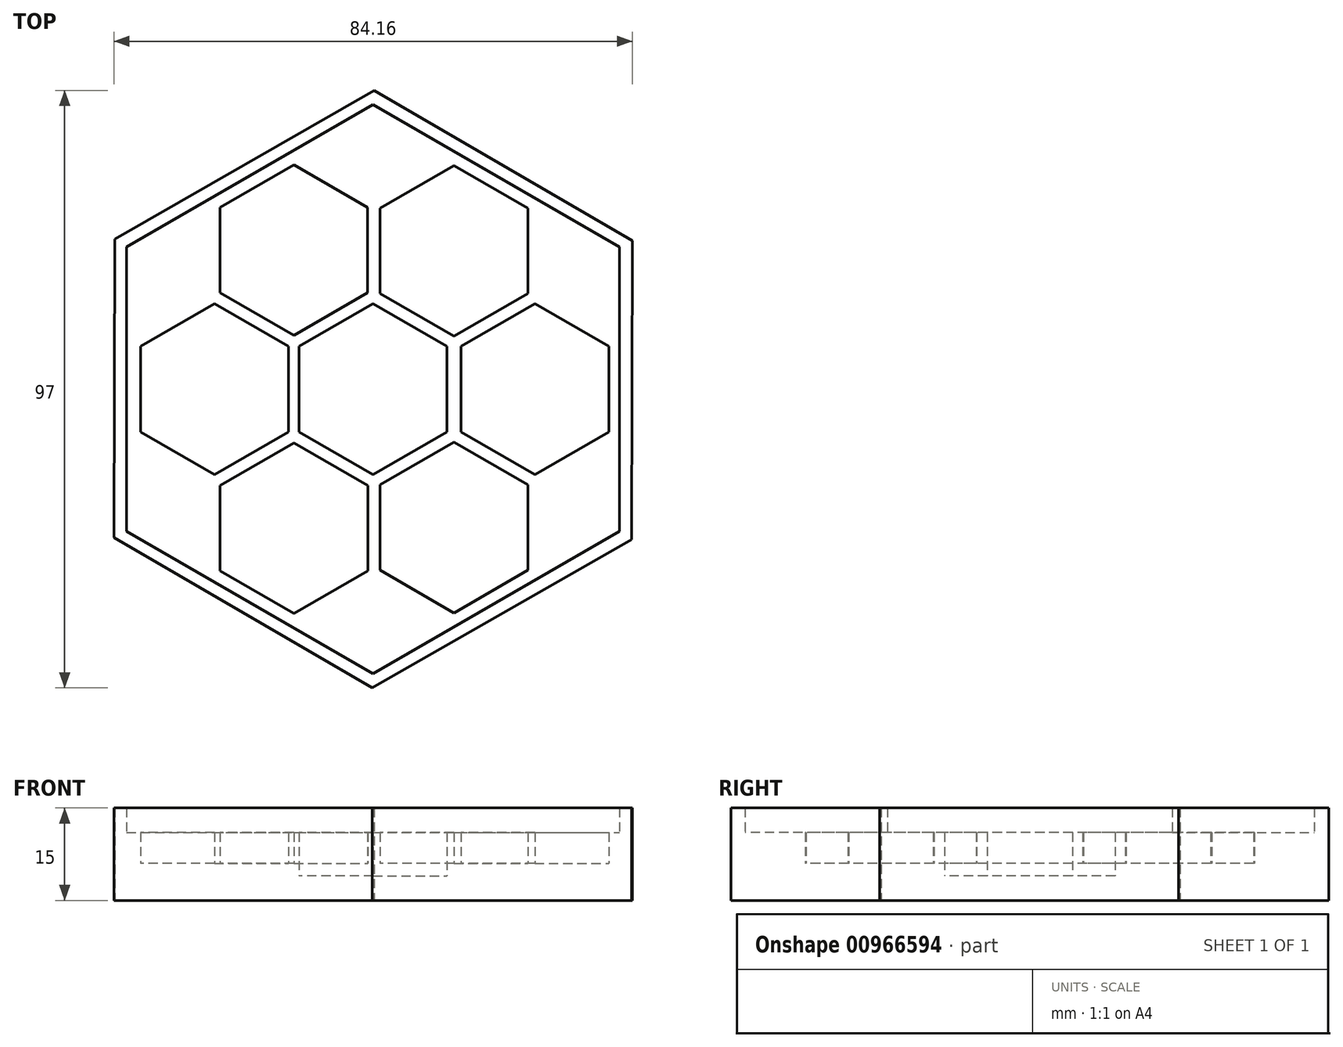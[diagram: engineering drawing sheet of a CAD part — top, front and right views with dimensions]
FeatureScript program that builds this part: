
annotation { "Feature Type Name" : "Feature", "Feature Type Description" : "" }
export const myFeature = defineFeature(function(context is Context, id is Id, definition is map)
    precondition{}
    {
        {
            var Q0;
            Q0=qCreatedBy(makeId("Top.planeOp"),FACE);
            var sketch = newSketch(context, id + "F0", { "sketchPlane" : qUnion([Q0])});
            skCircle(sketch, "E0.cCircle", {"center": v(0, 0) * mm, "radius": 12 * mm, "construction": true});
            skLineSegment(sketch, "E0.0", {"start": v(12, 6.93) * mm, "end": v(12, -6.93) * mm});
            skLineSegment(sketch, "E0.1", {"start": v(12, -6.93) * mm, "end": v(0, -13.86) * mm});
            skLineSegment(sketch, "E0.2", {"start": v(0, -13.86) * mm, "end": v(-12, -6.93) * mm});
            skLineSegment(sketch, "E0.3", {"start": v(-12, -6.93) * mm, "end": v(-12, 6.93) * mm});
            skLineSegment(sketch, "E0.4", {"start": v(-12, 6.93) * mm, "end": v(0, 13.86) * mm});
            skLineSegment(sketch, "E0.5", {"start": v(0, 13.86) * mm, "end": v(12, 6.93) * mm});
            skPoint(sketch, "E0.0.midPoint", {"position": v(12, 0) * mm});
            skCircle(sketch, "E1.cCircle", {"center": v(13.12, 22.45) * mm, "radius": 12 * mm, "construction": true});
            skLineSegment(sketch, "E1.0", {"start": v(25.12, 29.38) * mm, "end": v(25.12, 15.52) * mm});
            skLineSegment(sketch, "E1.1", {"start": v(25.12, 15.52) * mm, "end": v(13.12, 8.6) * mm});
            skLineSegment(sketch, "E1.2", {"start": v(13.12, 8.6) * mm, "end": v(1.12, 15.52) * mm});
            skLineSegment(sketch, "E1.3", {"start": v(1.12, 15.52) * mm, "end": v(1.12, 29.38) * mm});
            skLineSegment(sketch, "E1.4", {"start": v(1.12, 29.38) * mm, "end": v(13.12, 36.3) * mm});
            skLineSegment(sketch, "E1.5", {"start": v(13.12, 36.3) * mm, "end": v(25.12, 29.38) * mm});
            skPoint(sketch, "E1.0.midPoint", {"position": v(25.12, 22.45) * mm});
            skCircle(sketch, "E2.cCircle", {"center": v(-12.88, 22.58) * mm, "radius": 12 * mm, "construction": true});
            skLineSegment(sketch, "E2.0", {"start": v(-0.88, 29.51) * mm, "end": v(-0.88, 15.66) * mm});
            skLineSegment(sketch, "E2.1", {"start": v(-0.88, 15.66) * mm, "end": v(-12.88, 8.73) * mm});
            skLineSegment(sketch, "E2.2", {"start": v(-12.88, 8.73) * mm, "end": v(-24.88, 15.66) * mm});
            skLineSegment(sketch, "E2.3", {"start": v(-24.88, 15.66) * mm, "end": v(-24.88, 29.51) * mm});
            skLineSegment(sketch, "E2.4", {"start": v(-24.88, 29.51) * mm, "end": v(-12.88, 36.44) * mm});
            skLineSegment(sketch, "E2.5", {"start": v(-12.88, 36.44) * mm, "end": v(-0.88, 29.51) * mm});
            skPoint(sketch, "E2.0.midPoint", {"position": v(-0.88, 22.58) * mm});
            skCircle(sketch, "E3.cCircle", {"center": v(-25.77, 0) * mm, "radius": 12 * mm, "construction": true});
            skLineSegment(sketch, "E3.0", {"start": v(-13.77, 6.93) * mm, "end": v(-13.77, -6.93) * mm});
            skLineSegment(sketch, "E3.1", {"start": v(-13.77, -6.93) * mm, "end": v(-25.77, -13.86) * mm});
            skLineSegment(sketch, "E3.2", {"start": v(-25.77, -13.86) * mm, "end": v(-37.77, -6.93) * mm});
            skLineSegment(sketch, "E3.3", {"start": v(-37.77, -6.93) * mm, "end": v(-37.77, 6.93) * mm});
            skLineSegment(sketch, "E3.4", {"start": v(-37.77, 6.93) * mm, "end": v(-25.77, 13.86) * mm});
            skLineSegment(sketch, "E3.5", {"start": v(-25.77, 13.86) * mm, "end": v(-13.77, 6.93) * mm});
            skPoint(sketch, "E3.0.midPoint", {"position": v(-13.77, 0) * mm});
            skCircle(sketch, "E4.cCircle", {"center": v(13.14, -22.46) * mm, "radius": 12 * mm, "construction": true});
            skLineSegment(sketch, "E4.0", {"start": v(25.14, -15.54) * mm, "end": v(25.14, -29.4) * mm});
            skLineSegment(sketch, "E4.1", {"start": v(25.14, -29.4) * mm, "end": v(13.14, -36.32) * mm});
            skLineSegment(sketch, "E4.2", {"start": v(13.14, -36.32) * mm, "end": v(1.14, -29.4) * mm});
            skLineSegment(sketch, "E4.3", {"start": v(1.14, -29.4) * mm, "end": v(1.14, -15.54) * mm});
            skLineSegment(sketch, "E4.4", {"start": v(1.14, -15.54) * mm, "end": v(13.14, -8.6) * mm});
            skLineSegment(sketch, "E4.5", {"start": v(13.14, -8.6) * mm, "end": v(25.14, -15.54) * mm});
            skPoint(sketch, "E4.0.midPoint", {"position": v(25.14, -22.46) * mm});
            skCircle(sketch, "E5.cCircle", {"center": v(26.23, 0) * mm, "radius": 12 * mm, "construction": true});
            skLineSegment(sketch, "E5.0", {"start": v(38.23, 6.93) * mm, "end": v(38.23, -6.93) * mm});
            skLineSegment(sketch, "E5.1", {"start": v(38.23, -6.93) * mm, "end": v(26.23, -13.86) * mm});
            skLineSegment(sketch, "E5.2", {"start": v(26.23, -13.86) * mm, "end": v(14.23, -6.93) * mm});
            skLineSegment(sketch, "E5.3", {"start": v(14.23, -6.93) * mm, "end": v(14.23, 6.93) * mm});
            skLineSegment(sketch, "E5.4", {"start": v(14.23, 6.93) * mm, "end": v(26.23, 13.86) * mm});
            skLineSegment(sketch, "E5.5", {"start": v(26.23, 13.86) * mm, "end": v(38.23, 6.93) * mm});
            skPoint(sketch, "E5.0.midPoint", {"position": v(38.23, 0) * mm});
            skCircle(sketch, "E6.cCircle", {"center": v(-12.86, -22.57) * mm, "radius": 12 * mm, "construction": true});
            skLineSegment(sketch, "E6.0", {"start": v(-0.86, -15.64) * mm, "end": v(-0.86, -29.5) * mm});
            skLineSegment(sketch, "E6.1", {"start": v(-0.86, -29.5) * mm, "end": v(-12.86, -36.43) * mm});
            skLineSegment(sketch, "E6.2", {"start": v(-12.86, -36.43) * mm, "end": v(-24.86, -29.5) * mm});
            skLineSegment(sketch, "E6.3", {"start": v(-24.86, -29.5) * mm, "end": v(-24.86, -15.64) * mm});
            skLineSegment(sketch, "E6.4", {"start": v(-24.86, -15.64) * mm, "end": v(-12.86, -8.71) * mm});
            skLineSegment(sketch, "E6.5", {"start": v(-12.86, -8.71) * mm, "end": v(-0.86, -15.64) * mm});
            skPoint(sketch, "E6.0.midPoint", {"position": v(-0.86, -22.57) * mm});
            skCircle(sketch, "E7.cCircle", {"center": v(0, 0) * mm, "radius": 42 * mm, "construction": true});
            skLineSegment(sketch, "E7.0", {"start": v(0.16, 48.5) * mm, "end": v(42.08, 24.11) * mm});
            skLineSegment(sketch, "E7.1", {"start": v(42.08, 24.11) * mm, "end": v(41.92, -24.38) * mm});
            skLineSegment(sketch, "E7.2", {"start": v(41.92, -24.38) * mm, "end": v(-0.16, -48.5) * mm});
            skLineSegment(sketch, "E7.3", {"start": v(-0.16, -48.5) * mm, "end": v(-42.08, -24.11) * mm});
            skLineSegment(sketch, "E7.4", {"start": v(-42.08, -24.11) * mm, "end": v(-41.92, 24.38) * mm});
            skLineSegment(sketch, "E7.5", {"start": v(-41.92, 24.38) * mm, "end": v(0.16, 48.5) * mm});
            skPoint(sketch, "E7.0.midPoint", {"position": v(21.12, 36.3) * mm});
            skCircle(sketch, "E8.cCircle", {"center": v(0, 0) * mm, "radius": 40 * mm, "construction": true});
            skLineSegment(sketch, "E8.0", {"start": v(0, 46.19) * mm, "end": v(40, 23.1) * mm});
            skLineSegment(sketch, "E8.1", {"start": v(40, 23.1) * mm, "end": v(40, -23.1) * mm});
            skLineSegment(sketch, "E8.2", {"start": v(40, -23.1) * mm, "end": v(0, -46.19) * mm});
            skLineSegment(sketch, "E8.3", {"start": v(0, -46.19) * mm, "end": v(-40, -23.1) * mm});
            skLineSegment(sketch, "E8.4", {"start": v(-40, -23.1) * mm, "end": v(-40, 23.1) * mm});
            skLineSegment(sketch, "E8.5", {"start": v(-40, 23.1) * mm, "end": v(0, 46.19) * mm});
            skPoint(sketch, "E8.0.midPoint", {"position": v(20, 34.64) * mm});
            skSolve(sketch);
        }
        {
            var Q0;
            Q0=qSketchRegion(id+"F0",true);
            extrude(context, id + "F1", {"entities" : qUnion([Q0]), "depth" : 15 * mm, "offsetDistance" : 25.4 * mm});
        }
        {
            var Q0;
            Q0=makeQuery(id+"F0.imprint","IMPRINT",FACE,{"disambiguationData":[TD([[makeQuery(id+"F0.imprint","IMPRINT",EDGE,{"derivedFrom":sQuery(id+"F0.wireOp",EDGE,"E0.0")}),1.0]])]});
            extrude(context, id + "F2", {"entities" : qUnion([Q0]), "operationType" : NewBodyOperationType.ADD, "depth" : 11 * mm, "offsetDistance" : 25.4 * mm});
        }
        {
            var Q0;
            Q0=makeQuery(id+"F0.imprint","IMPRINT",FACE,{"disambiguationData":[TD([[makeQuery(id+"F0.imprint","IMPRINT",EDGE,{"derivedFrom":sQuery(id+"F0.wireOp",EDGE,"E1.0")}),-1.0]])]});
            var Q1;
            Q1=makeQuery(id+"F0.imprint","IMPRINT",FACE,{"disambiguationData":[TD([[makeQuery(id+"F0.imprint","IMPRINT",EDGE,{"derivedFrom":sQuery(id+"F0.wireOp",EDGE,"E2.0")}),-1.0]])]});
            var Q2;
            Q2=makeQuery(id+"F0.imprint","IMPRINT",FACE,{"disambiguationData":[TD([[makeQuery(id+"F0.imprint","IMPRINT",EDGE,{"derivedFrom":sQuery(id+"F0.wireOp",EDGE,"E3.0")}),-1.0]])]});
            var Q3;
            Q3=makeQuery(id+"F0.imprint","IMPRINT",FACE,{"disambiguationData":[TD([[makeQuery(id+"F0.imprint","IMPRINT",EDGE,{"derivedFrom":sQuery(id+"F0.wireOp",EDGE,"E0.0")}),-1.0]])]});
            var Q4;
            Q4=makeQuery(id+"F0.imprint","IMPRINT",FACE,{"disambiguationData":[TD([[makeQuery(id+"F0.imprint","IMPRINT",EDGE,{"derivedFrom":sQuery(id+"F0.wireOp",EDGE,"E5.0")}),-1.0]])]});
            var Q5;
            Q5=makeQuery(id+"F0.imprint","IMPRINT",FACE,{"disambiguationData":[TD([[makeQuery(id+"F0.imprint","IMPRINT",EDGE,{"derivedFrom":sQuery(id+"F0.wireOp",EDGE,"E4.0")}),-1.0]])]});
            var Q6;
            Q6=makeQuery(id+"F0.imprint","IMPRINT",FACE,{"disambiguationData":[TD([[makeQuery(id+"F0.imprint","IMPRINT",EDGE,{"derivedFrom":sQuery(id+"F0.wireOp",EDGE,"E6.0")}),-1.0]])]});
            extrude(context, id + "F3", {"entities" : qUnion([Q0, Q1, Q2, Q3, Q4, Q5, Q6]), "operationType" : NewBodyOperationType.ADD, "depth" : 4 * mm, "offsetDistance" : 25.4 * mm});
        }
        {
            var Q0;
            Q0=makeQuery(id+"F3.opExtrude","CAP_FACE",FACE,{"disambiguationData":[OSD([sQuery(id+"F0.wireOp",EDGE,"E3.0"),sQuery(id+"F0.wireOp",EDGE,"E3.1"),sQuery(id+"F0.wireOp",EDGE,"E3.2"),sQuery(id+"F0.wireOp",EDGE,"E3.3"),sQuery(id+"F0.wireOp",EDGE,"E3.4"),sQuery(id+"F0.wireOp",EDGE,"E3.5")])],"isStart":false});
            var Q1;
            Q1=makeQuery(id+"F3.opExtrude","CAP_FACE",FACE,{"disambiguationData":[OSD([sQuery(id+"F0.wireOp",EDGE,"E2.0"),sQuery(id+"F0.wireOp",EDGE,"E2.1"),sQuery(id+"F0.wireOp",EDGE,"E2.2"),sQuery(id+"F0.wireOp",EDGE,"E2.3"),sQuery(id+"F0.wireOp",EDGE,"E2.4"),sQuery(id+"F0.wireOp",EDGE,"E2.5")])],"isStart":false});
            var Q2;
            Q2=makeQuery(id+"F3.opExtrude","CAP_FACE",FACE,{"disambiguationData":[OSD([sQuery(id+"F0.wireOp",EDGE,"E1.0"),sQuery(id+"F0.wireOp",EDGE,"E1.1"),sQuery(id+"F0.wireOp",EDGE,"E1.2"),sQuery(id+"F0.wireOp",EDGE,"E1.3"),sQuery(id+"F0.wireOp",EDGE,"E1.4"),sQuery(id+"F0.wireOp",EDGE,"E1.5")])],"isStart":false});
            var Q3;
            Q3=makeQuery(id+"F3.opExtrude","CAP_FACE",FACE,{"disambiguationData":[OSD([sQuery(id+"F0.wireOp",EDGE,"E5.0"),sQuery(id+"F0.wireOp",EDGE,"E5.1"),sQuery(id+"F0.wireOp",EDGE,"E5.2"),sQuery(id+"F0.wireOp",EDGE,"E5.3"),sQuery(id+"F0.wireOp",EDGE,"E5.4"),sQuery(id+"F0.wireOp",EDGE,"E5.5")])],"isStart":false});
            var Q4;
            Q4=makeQuery(id+"F3.opExtrude","CAP_FACE",FACE,{"disambiguationData":[OSD([sQuery(id+"F0.wireOp",EDGE,"E4.0"),sQuery(id+"F0.wireOp",EDGE,"E4.1"),sQuery(id+"F0.wireOp",EDGE,"E4.2"),sQuery(id+"F0.wireOp",EDGE,"E4.3"),sQuery(id+"F0.wireOp",EDGE,"E4.4"),sQuery(id+"F0.wireOp",EDGE,"E4.5")])],"isStart":false});
            var Q5;
            Q5=makeQuery(id+"F3.opExtrude","CAP_FACE",FACE,{"disambiguationData":[OSD([sQuery(id+"F0.wireOp",EDGE,"E6.0"),sQuery(id+"F0.wireOp",EDGE,"E6.1"),sQuery(id+"F0.wireOp",EDGE,"E6.2"),sQuery(id+"F0.wireOp",EDGE,"E6.3"),sQuery(id+"F0.wireOp",EDGE,"E6.4"),sQuery(id+"F0.wireOp",EDGE,"E6.5")])],"isStart":false});
            extrude(context, id + "F4", {"entities" : qUnion([Q0, Q1, Q2, Q3, Q4, Q5]), "operationType" : NewBodyOperationType.ADD, "depth" : 2 * mm, "offsetDistance" : 25.4 * mm});
        }
    });
